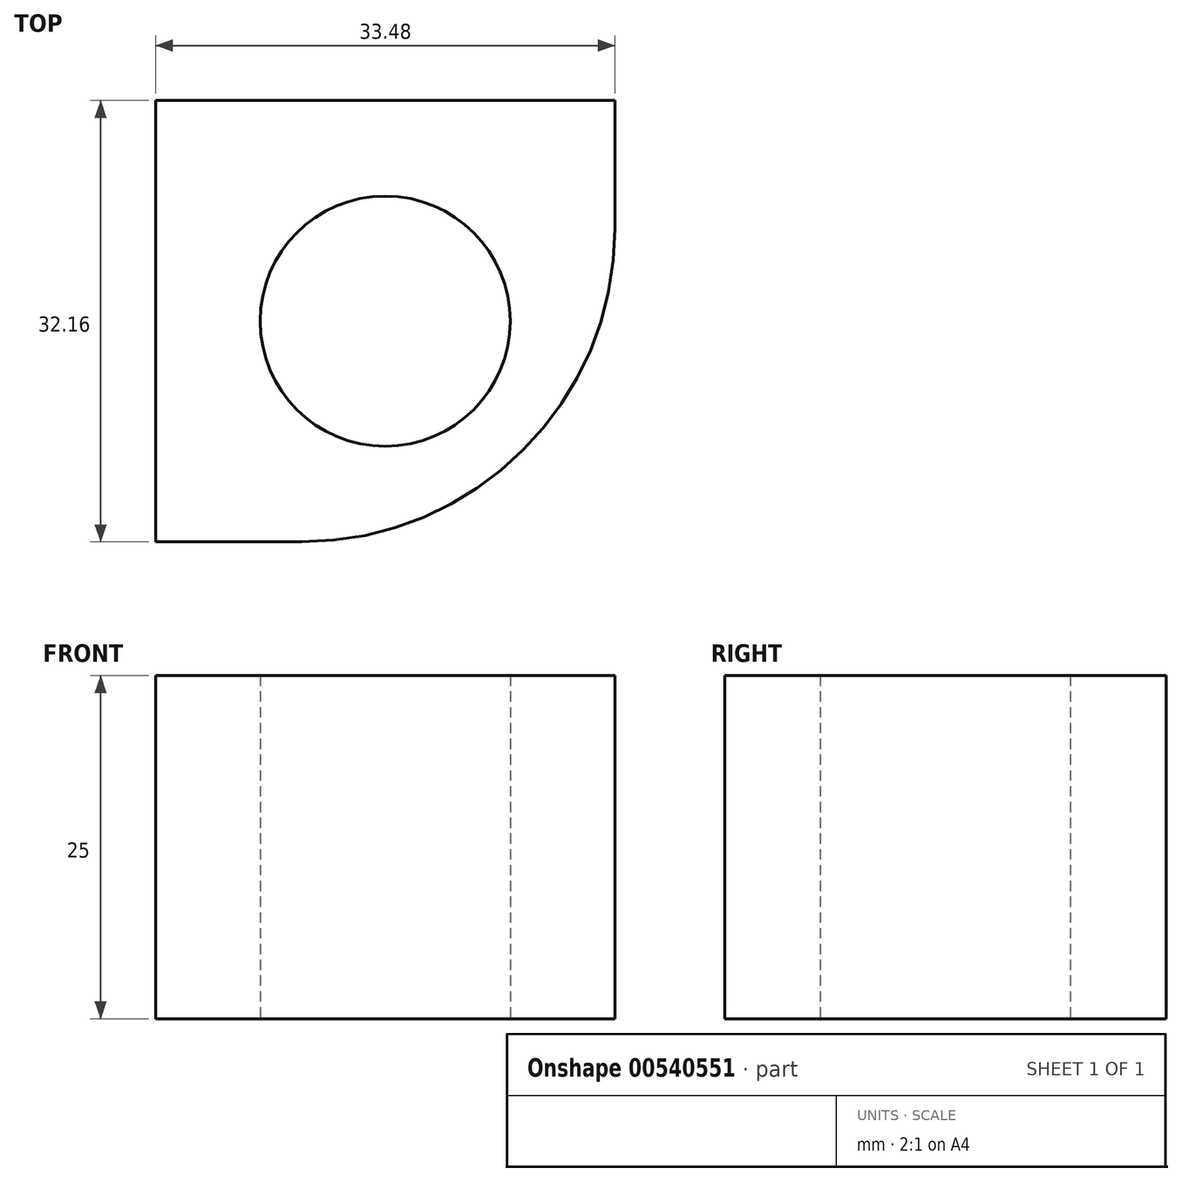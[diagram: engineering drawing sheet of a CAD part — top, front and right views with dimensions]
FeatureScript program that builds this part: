
annotation { "Feature Type Name" : "Feature", "Feature Type Description" : "" }
export const myFeature = defineFeature(function(context is Context, id is Id, definition is map)
    precondition{}
    {
        {
            var Q0;
            Q0=qCreatedBy(makeId("Top.planeOp"),FACE);
            var sketch = newSketch(context, id + "F0", { "sketchPlane" : qUnion([Q0])});
            skLineSegment(sketch, "E0.bottom", {"start": v(-16.74, 16.08) * mm, "end": v(16.74, 16.08) * mm});
            skLineSegment(sketch, "E0.top", {"start": v(-16.74, -16.08) * mm, "end": v(-6.1, -16.08) * mm});
            skLineSegment(sketch, "E0.left", {"start": v(-16.74, 16.08) * mm, "end": v(-16.74, -16.08) * mm});
            skLineSegment(sketch, "E0.right", {"start": v(16.74, 16.08) * mm, "end": v(16.74, 6.76) * mm});
            skPoint(sketch, "E0.middle", {"position": v(0, 0) * mm});
            skPoint(sketch, "E1.visualSharp", {"position": v(16.74, -16.08) * mm});
            skArc(sketch, "E1.filletArc", {"start": v(-6.1, -16.08) * mm, "mid": v(10.05, -9.4) * mm, "end": v(16.74, 6.76) * mm});
            skCircle(sketch, "E2", {"center": v(0, 0) * mm, "radius": 9.11 * mm});
            skSolve(sketch);
        }
        {
            var Q0;
            Q0=makeQuery(id+"F0.imprint","IMPRINT",FACE,{"disambiguationData":[TD([[makeQuery(id+"F0.imprint","IMPRINT",EDGE,{"derivedFrom":sQuery(id+"F0.wireOp",EDGE,"E0.bottom")}),-1.0]])]});
            extrude(context, id + "F1", {"entities" : qUnion([Q0]), "depth" : 25 * mm, "offsetDistance" : 25 * mm});
        }
    });
